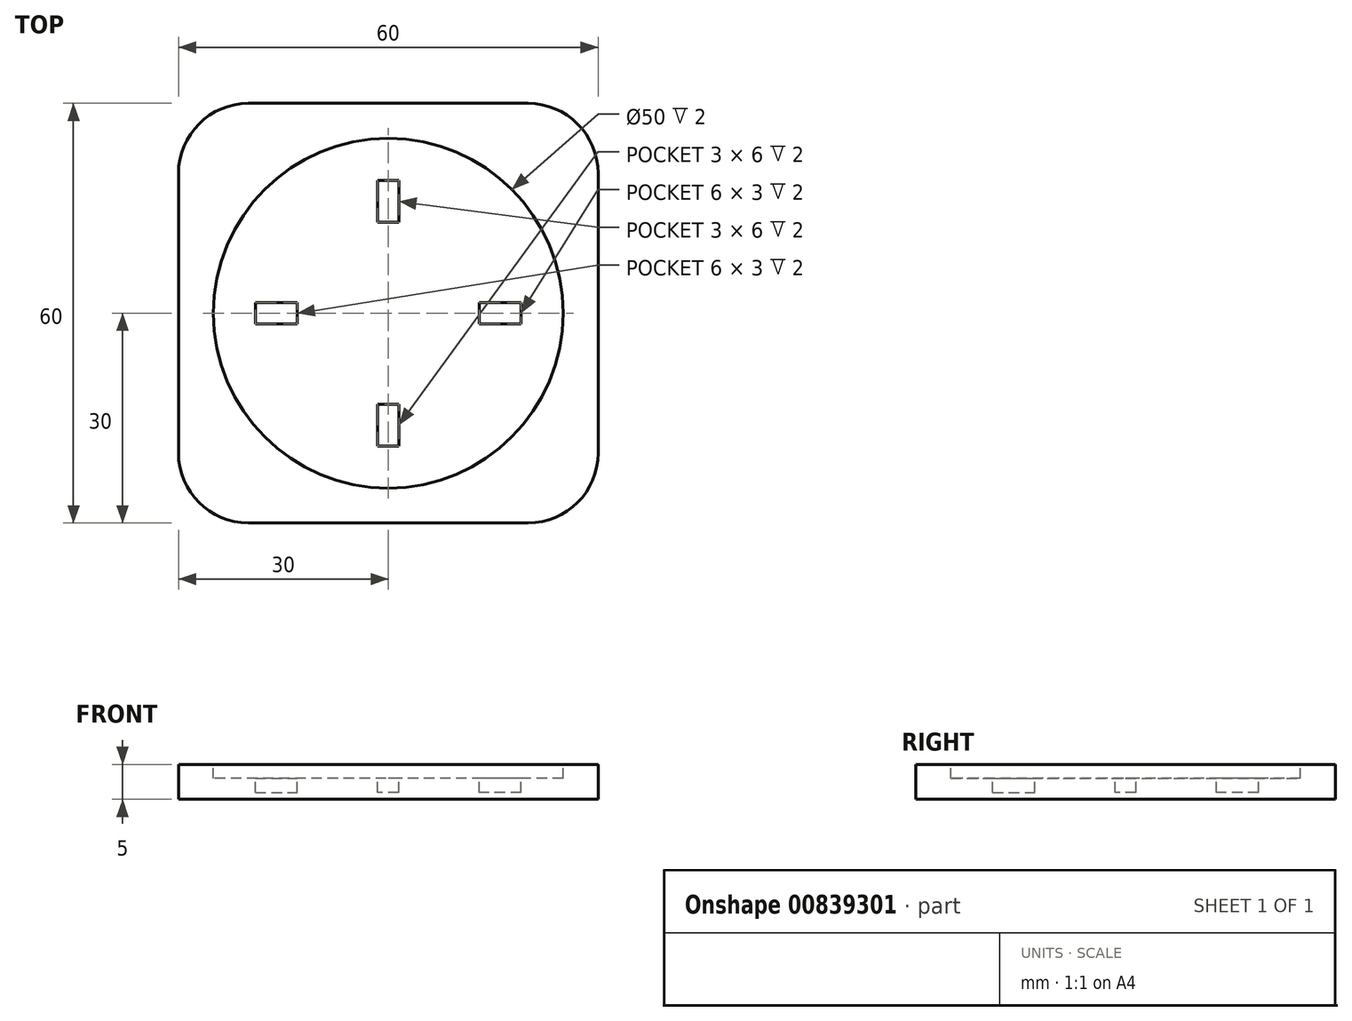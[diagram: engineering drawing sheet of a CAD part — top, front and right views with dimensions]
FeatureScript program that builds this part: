
annotation { "Feature Type Name" : "Feature", "Feature Type Description" : "" }
export const myFeature = defineFeature(function(context is Context, id is Id, definition is map)
    precondition{}
    {
        {
            var Q0;
            Q0=qCreatedBy(makeId("Top.planeOp"),FACE);
            var sketch = newSketch(context, id + "F0", { "sketchPlane" : qUnion([Q0])});
            skLineSegment(sketch, "E0.bottom", {"start": v(30, -30) * mm, "end": v(-30, -30) * mm});
            skLineSegment(sketch, "E0.top", {"start": v(30, 30) * mm, "end": v(-30, 30) * mm});
            skLineSegment(sketch, "E0.left", {"start": v(30, -30) * mm, "end": v(30, 30) * mm});
            skLineSegment(sketch, "E0.right", {"start": v(-30, -30) * mm, "end": v(-30, 30) * mm});
            skPoint(sketch, "E0.middle", {"position": v(0, 0) * mm});
            skSolve(sketch);
        }
        {
            var Q0;
            Q0=makeQuery(id+"F0.imprint","IMPRINT",FACE,{"disambiguationData":[TD([[makeQuery(id+"F0.imprint","IMPRINT",EDGE,{"derivedFrom":sQuery(id+"F0.wireOp",EDGE,"E0.bottom")}),-1.0]])]});
            extrude(context, id + "F1", {"entities" : qUnion([Q0]), "depth" : 5 * mm, "offsetDistance" : 25 * mm});
        }
        {
            var Q0;
            Q0=makeQuery(id+"F1.opExtrude","CAP_FACE",FACE,{"disambiguationData":[OSD([sQuery(id+"F0.wireOp",EDGE,"E0.bottom"),sQuery(id+"F0.wireOp",EDGE,"E0.top"),sQuery(id+"F0.wireOp",EDGE,"E0.left"),sQuery(id+"F0.wireOp",EDGE,"E0.right")])],"isStart":false});
            var sketch = newSketch(context, id + "F2", { "sketchPlane" : qUnion([Q0])});
            skCircle(sketch, "E1", {"center": v(0, 0) * mm, "radius": 25 * mm});
            skSolve(sketch);
        }
        {
            var Q0;
            Q0 = qSketchRegion(id + "F2", true);
            extrude(context, id + "F3", {"entities" : qUnion([Q0]), "operationType" : NewBodyOperationType.REMOVE, "oppositeDirection" : true, "depth" : 2 * mm, "offsetDistance" : 25 * mm});
        }
        {
            var Q0;
            Q0=makeQuery(id+"F1.opExtrude","SWEPT_EDGE",EDGE,{"disambiguationData":[OSD([sQuery(id+"F0.wireOp",EDGE,"E0.bottom"),sQuery(id+"F0.wireOp",EDGE,"E0.right")])]});
            fillet(context, id + "F4", {"entities" : qUnion([Q0]), "radius" : 10 * mm, "tangentPropagation" : true, "allowEdgeOverflow" : false});
        }
        {
            var Q0;
            Q0=makeQuery(id+"F1.opExtrude","SWEPT_EDGE",EDGE,{"disambiguationData":[OSD([sQuery(id+"F0.wireOp",EDGE,"E0.bottom"),sQuery(id+"F0.wireOp",EDGE,"E0.left")])]});
            var Q1;
            Q1=makeQuery(id+"F1.opExtrude","SWEPT_EDGE",EDGE,{"disambiguationData":[OSD([sQuery(id+"F0.wireOp",EDGE,"E0.top"),sQuery(id+"F0.wireOp",EDGE,"E0.left")])]});
            var Q2;
            Q2=makeQuery(id+"F1.opExtrude","SWEPT_EDGE",EDGE,{"disambiguationData":[OSD([sQuery(id+"F0.wireOp",EDGE,"E0.top"),sQuery(id+"F0.wireOp",EDGE,"E0.right")])]});
            fillet(context, id + "F5", {"entities" : qUnion([Q0, Q1, Q2]), "radius" : 10 * mm, "tangentPropagation" : true, "allowEdgeOverflow" : false});
        }
        {
            var Q0;
            Q0=makeQuery(id+"F3.boolean.opBoolean","COPY",FACE,{"derivedFrom":makeQuery(id+"F3.opExtrude","CAP_FACE",FACE,{"disambiguationData":[OSD([sQuery(id+"F2.wireOp",EDGE,"E1")])],"isStart":false})});
            var sketch = newSketch(context, id + "F6", { "sketchPlane" : qUnion([Q0])});
            skLineSegment(sketch, "E2.bottom", {"start": v(-1.5, 19) * mm, "end": v(1.5, 19) * mm});
            skLineSegment(sketch, "E2.top", {"start": v(-1.5, 13) * mm, "end": v(1.5, 13) * mm});
            skLineSegment(sketch, "E2.left", {"start": v(-1.5, 19) * mm, "end": v(-1.5, 13) * mm});
            skLineSegment(sketch, "E2.right", {"start": v(1.5, 19) * mm, "end": v(1.5, 13) * mm});
            skPoint(sketch, "E3.center", {"position": v(0, 0) * mm});
            skLineSegment(sketch, "E4.1.0", {"start": v(-19, 1.5) * mm, "end": v(-13, 1.5) * mm});
            skLineSegment(sketch, "E4.1.1", {"start": v(-19, -1.5) * mm, "end": v(-13, -1.5) * mm});
            skLineSegment(sketch, "E4.1.2", {"start": v(-19, -1.5) * mm, "end": v(-19, 1.5) * mm});
            skLineSegment(sketch, "E4.1.3", {"start": v(-13, -1.5) * mm, "end": v(-13, 1.5) * mm});
            skLineSegment(sketch, "E4.2.0", {"start": v(-1.5, -19) * mm, "end": v(-1.5, -13) * mm});
            skLineSegment(sketch, "E4.2.1", {"start": v(1.5, -19) * mm, "end": v(1.5, -13) * mm});
            skLineSegment(sketch, "E4.2.2", {"start": v(1.5, -19) * mm, "end": v(-1.5, -19) * mm});
            skLineSegment(sketch, "E4.2.3", {"start": v(1.5, -13) * mm, "end": v(-1.5, -13) * mm});
            skLineSegment(sketch, "E4.3.0", {"start": v(19, -1.5) * mm, "end": v(13, -1.5) * mm});
            skLineSegment(sketch, "E4.3.1", {"start": v(19, 1.5) * mm, "end": v(13, 1.5) * mm});
            skLineSegment(sketch, "E4.3.2", {"start": v(19, 1.5) * mm, "end": v(19, -1.5) * mm});
            skLineSegment(sketch, "E4.3.3", {"start": v(13, 1.5) * mm, "end": v(13, -1.5) * mm});
            skLineSegment(sketch, "E4.anchor1", {"start": v(0, 0) * mm, "end": v(1.5, 13) * mm, "construction": true});
            skLineSegment(sketch, "E4.anchor2", {"start": v(0, 0) * mm, "end": v(13, -1.5) * mm, "construction": true});
            skSolve(sketch);
        }
        {
            var Q0;
            Q0=makeQuery(id+"F6.imprint","IMPRINT",FACE,{"disambiguationData":[TD([[makeQuery(id+"F6.imprint","IMPRINT",EDGE,{"derivedFrom":sQuery(id+"F6.wireOp",EDGE,"E4.1.0")}),-1.0]])]});
            var Q1;
            Q1=makeQuery(id+"F6.imprint","IMPRINT",FACE,{"disambiguationData":[TD([[makeQuery(id+"F6.imprint","IMPRINT",EDGE,{"derivedFrom":sQuery(id+"F6.wireOp",EDGE,"E2.bottom")}),-1.0]])]});
            var Q2;
            Q2=makeQuery(id+"F6.imprint","IMPRINT",FACE,{"disambiguationData":[TD([[makeQuery(id+"F6.imprint","IMPRINT",EDGE,{"derivedFrom":sQuery(id+"F6.wireOp",EDGE,"E4.3.0")}),-1.0]])]});
            var Q3;
            Q3=makeQuery(id+"F6.imprint","IMPRINT",FACE,{"disambiguationData":[TD([[makeQuery(id+"F6.imprint","IMPRINT",EDGE,{"derivedFrom":sQuery(id+"F6.wireOp",EDGE,"E4.2.0")}),-1.0]])]});
            extrude(context, id + "F7", {"entities" : qUnion([Q0, Q1, Q2, Q3]), "operationType" : NewBodyOperationType.REMOVE, "oppositeDirection" : true, "depth" : 2 * mm, "offsetDistance" : 25 * mm});
        }
    });
